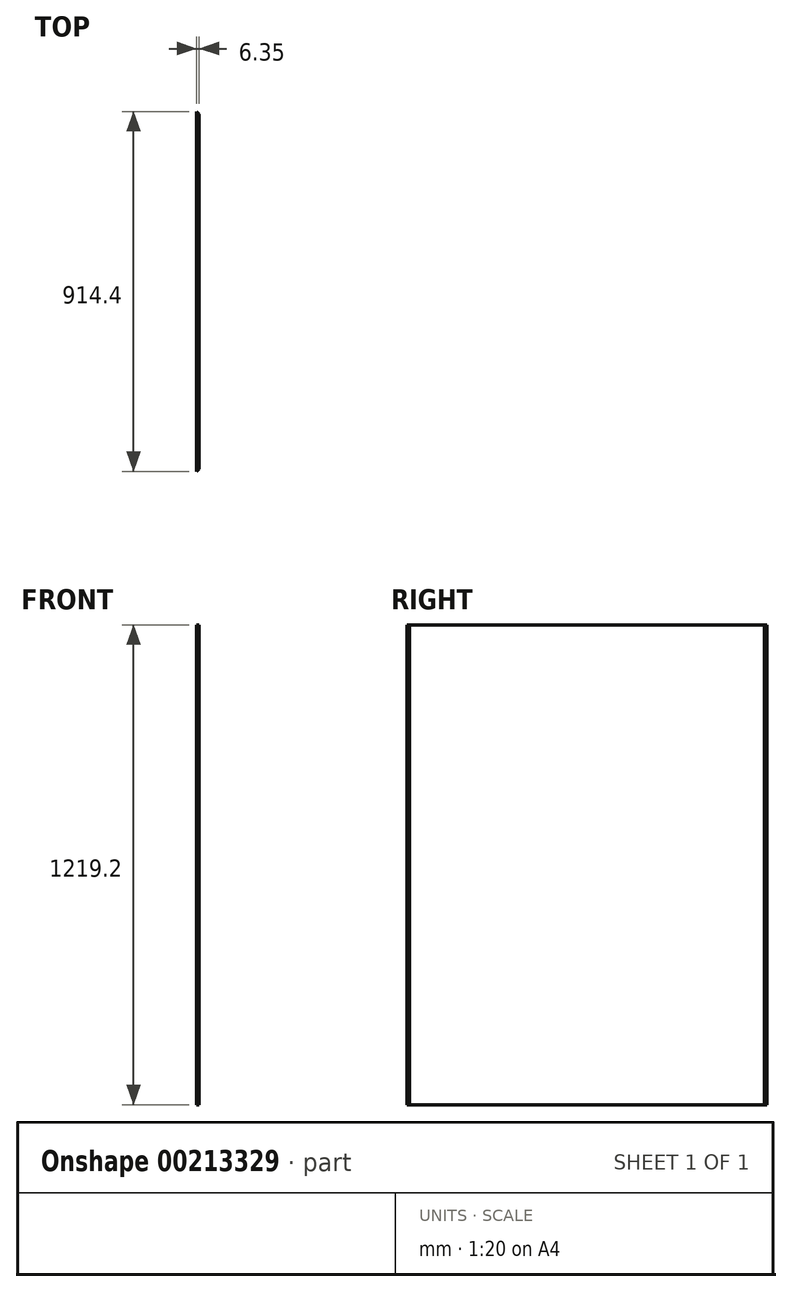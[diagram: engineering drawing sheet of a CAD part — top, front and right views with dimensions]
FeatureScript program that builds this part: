
annotation { "Feature Type Name" : "Feature", "Feature Type Description" : "" }
export const myFeature = defineFeature(function(context is Context, id is Id, definition is map)
    precondition{}
    {
        {
            var Q0;
            Q0=qCreatedBy(makeId("Right.planeOp"),FACE);
            var sketch = newSketch(context, id + "F0", { "sketchPlane" : qUnion([Q0])});
            skLineSegment(sketch, "E0.bottom", {"start": v(457.2, 609.6) * mm, "end": v(-457.2, 609.6) * mm});
            skLineSegment(sketch, "E0.top", {"start": v(457.2, -609.6) * mm, "end": v(-457.2, -609.6) * mm});
            skLineSegment(sketch, "E0.left", {"start": v(457.2, 609.6) * mm, "end": v(457.2, -609.6) * mm});
            skLineSegment(sketch, "E0.right", {"start": v(-457.2, 609.6) * mm, "end": v(-457.2, -609.6) * mm});
            skPoint(sketch, "E0.middle", {"position": v(0, 0) * mm});
            skSolve(sketch);
        }
        {
            var Q0;
            Q0=makeQuery(id+"F0.imprint","IMPRINT",FACE,{"disambiguationData":[TD([[makeQuery(id+"F0.imprint","IMPRINT",EDGE,{"derivedFrom":sQuery(id+"F0.wireOp",EDGE,"E0.bottom")}),1.0]])]});
            extrude(context, id + "F1", {"entities" : qUnion([Q0]), "depth" : 6.35 * mm});
        }
        {
            var Q0;
            Q0=makeQuery(id+"F1.opExtrude","CAP_EDGE",EDGE,{"disambiguationData":[OSD([sQuery(id+"F0.wireOp",EDGE,"E0.left")])],"isStart":false});
            chamfer(context, id + "F2", {"entities" : qUnion([Q0]), "width" : 6.35 * mm, "tangentPropagation" : true});
        }
        {
            var Q0;
            Q0=makeQuery(id+"F1.opExtrude","CAP_EDGE",EDGE,{"disambiguationData":[OSD([sQuery(id+"F0.wireOp",EDGE,"E0.right")])],"isStart":false});
            chamfer(context, id + "F3", {"entities" : qUnion([Q0]), "width" : 6.35 * mm, "tangentPropagation" : true});
        }
    });
